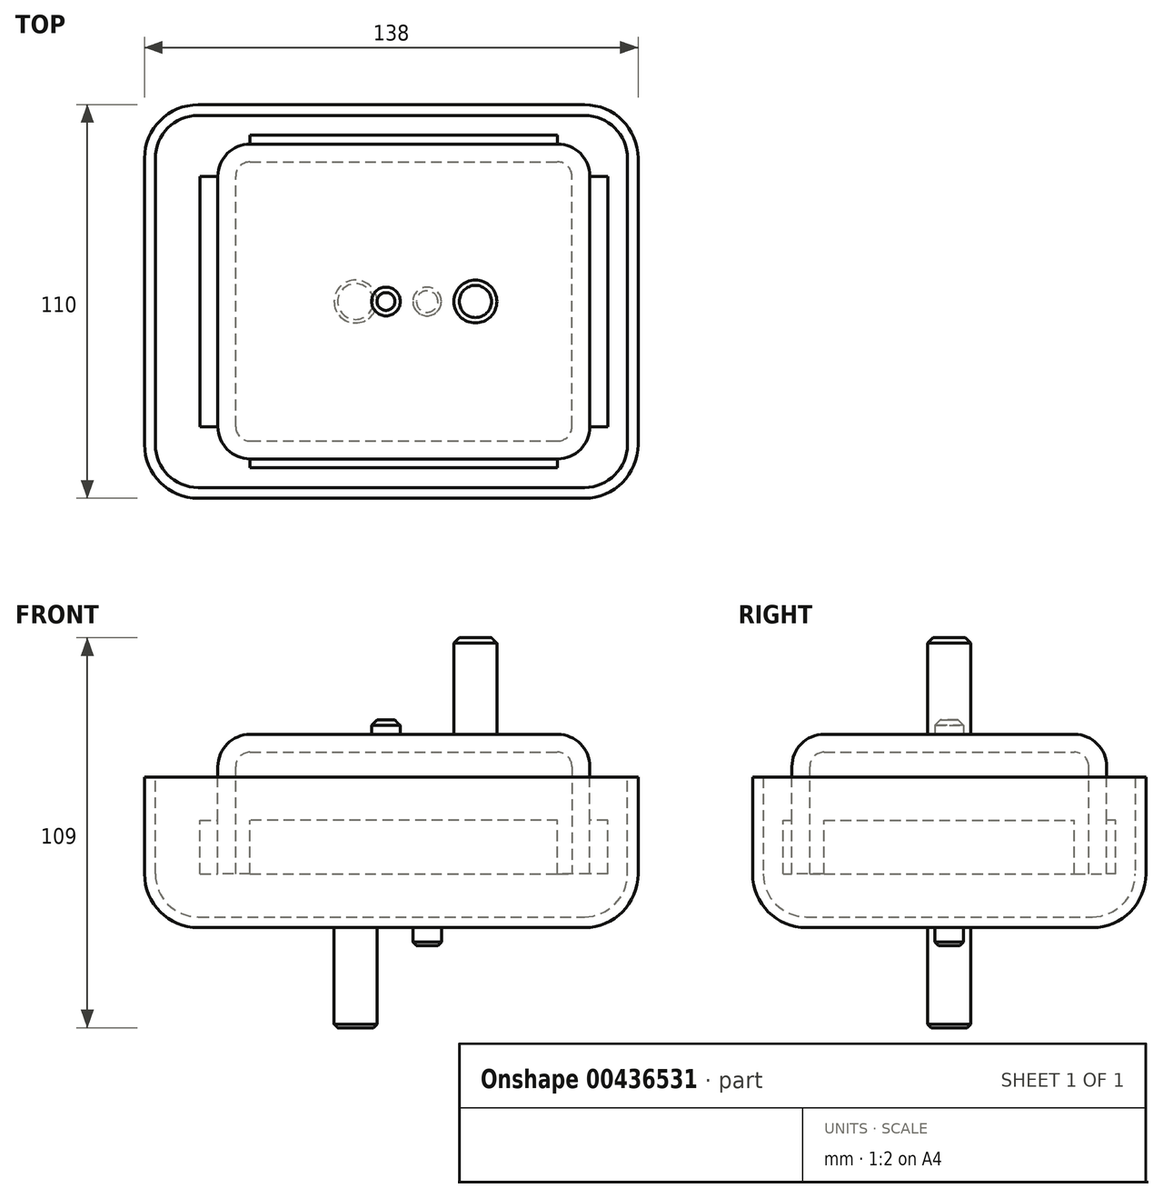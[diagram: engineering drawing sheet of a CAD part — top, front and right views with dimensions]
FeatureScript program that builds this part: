
annotation { "Feature Type Name" : "Feature", "Feature Type Description" : "" }
export const myFeature = defineFeature(function(context is Context, id is Id, definition is map)
    precondition{}
    {
        {
            var Q0;
            Q0=qCreatedBy(makeId("Top.planeOp"),FACE);
            var sketch = newSketch(context, id + "F0", { "sketchPlane" : qUnion([Q0])});
            skLineSegment(sketch, "E0.bottom", {"start": v(54, -55) * mm, "end": v(-54, -55) * mm});
            skLineSegment(sketch, "E0.top", {"start": v(54, 55) * mm, "end": v(-54, 55) * mm});
            skLineSegment(sketch, "E0.left", {"start": v(69, -40) * mm, "end": v(69, 40) * mm});
            skLineSegment(sketch, "E0.right", {"start": v(-69, -40) * mm, "end": v(-69, 40) * mm});
            skPoint(sketch, "E0.middle", {"position": v(0, 0) * mm});
            skPoint(sketch, "E1.visualSharp", {"position": v(-69, 55) * mm});
            skArc(sketch, "E1.filletArc", {"start": v(-54, 55) * mm, "mid": v(-64.6, 50.6) * mm, "end": v(-69, 40) * mm});
            skPoint(sketch, "E2.visualSharp", {"position": v(69, 55) * mm});
            skArc(sketch, "E2.filletArc", {"start": v(69, 40) * mm, "mid": v(64.6, 50.6) * mm, "end": v(54, 55) * mm});
            skPoint(sketch, "E3.visualSharp", {"position": v(69, -55) * mm});
            skArc(sketch, "E3.filletArc", {"start": v(54, -55) * mm, "mid": v(64.6, -50.6) * mm, "end": v(69, -40) * mm});
            skPoint(sketch, "E4.visualSharp", {"position": v(-69, -55) * mm});
            skArc(sketch, "E4.filletArc", {"start": v(-69, -40) * mm, "mid": v(-64.6, -50.6) * mm, "end": v(-54, -55) * mm});
            skSolve(sketch);
        }
        {
            var Q0;
            Q0 = qSketchRegion(id + "F0", true);
            extrude(context, id + "F1", {"entities" : qUnion([Q0]), "depth" : 42 * mm});
        }
        {
            var Q0;
            Q0=makeQuery(id+"F1.opExtrude","CAP_EDGE",EDGE,{"disambiguationData":[OSD([sQuery(id+"F0.wireOp",EDGE,"E0.bottom")])],"isStart":true});
            fillet(context, id + "F2", {"entities" : qUnion([Q0]), "radius" : 15 * mm, "tangentPropagation" : true, "allowEdgeOverflow" : false});
        }
        {
            var Q0;
            Q0=makeQuery(id+"F1.opExtrude","CAP_FACE",FACE,{"disambiguationData":[OSD([sQuery(id+"F0.wireOp",EDGE,"E0.bottom"),sQuery(id+"F0.wireOp",EDGE,"E0.top"),sQuery(id+"F0.wireOp",EDGE,"E0.left"),sQuery(id+"F0.wireOp",EDGE,"E0.right"),sQuery(id+"F0.wireOp",EDGE,"E1.filletArc"),sQuery(id+"F0.wireOp",EDGE,"E2.filletArc"),sQuery(id+"F0.wireOp",EDGE,"E3.filletArc"),sQuery(id+"F0.wireOp",EDGE,"E4.filletArc")])],"isStart":false});
            shell(context, id + "F3", {"entities" : qUnion([Q0]), "thickness" : 3 * mm});
        }
        {
            var Q0;
            Q0=makeQuery(id+"F1.opExtrude","CAP_FACE",FACE,{"disambiguationData":[OSD([sQuery(id+"F0.wireOp",EDGE,"E0.bottom"),sQuery(id+"F0.wireOp",EDGE,"E0.top"),sQuery(id+"F0.wireOp",EDGE,"E0.left"),sQuery(id+"F0.wireOp",EDGE,"E0.right"),sQuery(id+"F0.wireOp",EDGE,"E1.filletArc"),sQuery(id+"F0.wireOp",EDGE,"E2.filletArc"),sQuery(id+"F0.wireOp",EDGE,"E3.filletArc"),sQuery(id+"F0.wireOp",EDGE,"E4.filletArc")])],"isStart":true});
            var sketch = newSketch(context, id + "F4", { "sketchPlane" : qUnion([Q0])});
            skCircle(sketch, "E5", {"center": v(-10, 0) * mm, "radius": 6 * mm});
            skCircle(sketch, "E6", {"center": v(10, 0) * mm, "radius": 4 * mm});
            skSolve(sketch);
        }
        {
            var Q0;
            Q0=makeQuery(id+"F4.imprint","IMPRINT",FACE,{"disambiguationData":[TD([[makeQuery(id+"F4.imprint","IMPRINT",EDGE,{"derivedFrom":sQuery(id+"F4.wireOp",EDGE,"E5")}),1.0]])]});
            extrude(context, id + "F5", {"entities" : qUnion([Q0]), "operationType" : NewBodyOperationType.ADD, "depth" : 28 * mm});
        }
        {
            var Q0;
            Q0=makeQuery(id+"F4.imprint","IMPRINT",FACE,{"disambiguationData":[TD([[makeQuery(id+"F4.imprint","IMPRINT",EDGE,{"derivedFrom":sQuery(id+"F4.wireOp",EDGE,"E6")}),1.0]])]});
            extrude(context, id + "F6", {"entities" : qUnion([Q0]), "operationType" : NewBodyOperationType.ADD, "depth" : 5 * mm});
        }
        {
            var Q0;
            Q0=makeQuery(id+"F6.opExtrude","CAP_EDGE",EDGE,{"disambiguationData":[OSD([sQuery(id+"F4.wireOp",EDGE,"E6")])],"isStart":false});
            var Q1;
            Q1=makeQuery(id+"F5.opExtrude","CAP_EDGE",EDGE,{"disambiguationData":[OSD([sQuery(id+"F4.wireOp",EDGE,"E5")])],"isStart":false});
            chamfer(context, id + "F7", {"entities" : qUnion([Q0, Q1]), "width" : 1 * mm, "tangentPropagation" : true});
        }
        {
            var Q0;
            Q0=qCreatedBy(makeId("Top.planeOp"),FACE);
            cPlane(context, id + "F8", {"entities" : qUnion([Q0]), "cplaneType" : CPlaneType.OFFSET, "offset" : 54 * mm, "width" : 150 * mm, "height" : 150 * mm});
        }
        {
            var Q0;
            Q0=qCreatedBy(id+"F8.planeOp",FACE);
            var sketch = newSketch(context, id + "F9", { "sketchPlane" : qUnion([Q0])});
            skLineSegment(sketch, "E7.bottom", {"start": v(-39.5, -44) * mm, "end": v(46.5, -44) * mm});
            skLineSegment(sketch, "E7.top", {"start": v(-39.5, 44) * mm, "end": v(46.5, 44) * mm});
            skLineSegment(sketch, "E7.left", {"start": v(-48.5, -35) * mm, "end": v(-48.5, 35) * mm});
            skLineSegment(sketch, "E7.right", {"start": v(55.5, -35) * mm, "end": v(55.5, 35) * mm});
            skPoint(sketch, "E8.visualSharp", {"position": v(-48.5, 44) * mm});
            skArc(sketch, "E8.filletArc", {"start": v(-39.5, 44) * mm, "mid": v(-45.86, 41.36) * mm, "end": v(-48.5, 35) * mm});
            skPoint(sketch, "E9.visualSharp", {"position": v(55.5, 44) * mm});
            skArc(sketch, "E9.filletArc", {"start": v(55.5, 35) * mm, "mid": v(52.86, 41.36) * mm, "end": v(46.5, 44) * mm});
            skPoint(sketch, "E10.visualSharp", {"position": v(55.5, -44) * mm});
            skArc(sketch, "E10.filletArc", {"start": v(46.5, -44) * mm, "mid": v(52.86, -41.36) * mm, "end": v(55.5, -35) * mm});
            skPoint(sketch, "E11.visualSharp", {"position": v(-48.5, -44) * mm});
            skArc(sketch, "E11.filletArc", {"start": v(-48.5, -35) * mm, "mid": v(-45.86, -41.36) * mm, "end": v(-39.5, -44) * mm});
            skSolve(sketch);
        }
        {
            var Q0;
            Q0 = qSketchRegion(id + "F9", true);
            extrude(context, id + "F10", {"entities" : qUnion([Q0]), "oppositeDirection" : true, "depth" : 39 * mm});
        }
        {
            var Q0;
            Q0=makeQuery(id+"F10.opExtrude","CAP_EDGE",EDGE,{"disambiguationData":[OSD([sQuery(id+"F9.wireOp",EDGE,"E7.left")])],"isStart":true});
            fillet(context, id + "F11", {"entities" : qUnion([Q0]), "radius" : 9 * mm, "tangentPropagation" : true, "allowEdgeOverflow" : false});
        }
        {
            var Q0;
            Q0=makeQuery(id+"F10.opExtrude","CAP_FACE",FACE,{"disambiguationData":[OSD([sQuery(id+"F9.wireOp",EDGE,"E7.bottom"),sQuery(id+"F9.wireOp",EDGE,"E7.top"),sQuery(id+"F9.wireOp",EDGE,"E7.left"),sQuery(id+"F9.wireOp",EDGE,"E7.right"),sQuery(id+"F9.wireOp",EDGE,"E8.filletArc"),sQuery(id+"F9.wireOp",EDGE,"E9.filletArc"),sQuery(id+"F9.wireOp",EDGE,"E10.filletArc"),sQuery(id+"F9.wireOp",EDGE,"E11.filletArc")])],"isStart":false});
            shell(context, id + "F12", {"entities" : qUnion([Q0]), "thickness" : 5 * mm});
        }
        {
            var Q0;
            Q0=makeQuery(id+"F10.opExtrude","SWEPT_FACE",FACE,{"disambiguationData":[OSD([sQuery(id+"F9.wireOp",EDGE,"E7.bottom")])]});
            var sketch = newSketch(context, id + "F13", { "sketchPlane" : qUnion([Q0])});
            skLineSegment(sketch, "E12.bottom", {"start": v(-39.5, 15) * mm, "end": v(46.5, 15) * mm});
            skLineSegment(sketch, "E12.top", {"start": v(-39.5, 30) * mm, "end": v(46.5, 30) * mm});
            skLineSegment(sketch, "E12.left", {"start": v(-39.5, 15) * mm, "end": v(-39.5, 30) * mm});
            skLineSegment(sketch, "E12.right", {"start": v(46.5, 15) * mm, "end": v(46.5, 30) * mm});
            skSolve(sketch);
        }
        {
            var Q0;
            Q0 = qSketchRegion(id + "F13", true);
            extrude(context, id + "F14", {"entities" : qUnion([Q0]), "operationType" : NewBodyOperationType.ADD, "depth" : 2.5 * mm});
        }
        {
            var Q0;
            Q0=makeQuery(id+"F10.opExtrude","SWEPT_FACE",FACE,{"disambiguationData":[OSD([sQuery(id+"F9.wireOp",EDGE,"E7.top")])]});
            var sketch = newSketch(context, id + "F15", { "sketchPlane" : qUnion([Q0])});
            skLineSegment(sketch, "E13.bottom", {"start": v(-46.5, 15) * mm, "end": v(39.5, 15) * mm});
            skLineSegment(sketch, "E13.top", {"start": v(-46.5, 30) * mm, "end": v(39.5, 30) * mm});
            skLineSegment(sketch, "E13.left", {"start": v(-46.5, 15) * mm, "end": v(-46.5, 30) * mm});
            skLineSegment(sketch, "E13.right", {"start": v(39.5, 15) * mm, "end": v(39.5, 30) * mm});
            skSolve(sketch);
        }
        {
            var Q0;
            Q0 = qSketchRegion(id + "F15", true);
            extrude(context, id + "F16", {"entities" : qUnion([Q0]), "operationType" : NewBodyOperationType.ADD, "depth" : 2.5 * mm});
        }
        {
            var Q0;
            Q0=makeQuery(id+"F10.opExtrude","SWEPT_FACE",FACE,{"disambiguationData":[OSD([sQuery(id+"F9.wireOp",EDGE,"E7.left")])]});
            var sketch = newSketch(context, id + "F17", { "sketchPlane" : qUnion([Q0])});
            skLineSegment(sketch, "E14.bottom", {"start": v(35, 15) * mm, "end": v(-35, 15) * mm});
            skLineSegment(sketch, "E14.top", {"start": v(35, 30) * mm, "end": v(-35, 30) * mm});
            skLineSegment(sketch, "E14.left", {"start": v(35, 15) * mm, "end": v(35, 30) * mm});
            skLineSegment(sketch, "E14.right", {"start": v(-35, 15) * mm, "end": v(-35, 30) * mm});
            skSolve(sketch);
        }
        {
            var Q0;
            Q0 = qSketchRegion(id + "F17", true);
            extrude(context, id + "F18", {"entities" : qUnion([Q0]), "operationType" : NewBodyOperationType.ADD, "depth" : 5 * mm});
        }
        {
            var Q0;
            Q0=makeQuery(id+"F10.opExtrude","SWEPT_FACE",FACE,{"disambiguationData":[OSD([sQuery(id+"F9.wireOp",EDGE,"E7.right")])]});
            var sketch = newSketch(context, id + "F19", { "sketchPlane" : qUnion([Q0])});
            skLineSegment(sketch, "E15.bottom", {"start": v(-35, 15) * mm, "end": v(35, 15) * mm});
            skLineSegment(sketch, "E15.top", {"start": v(-35, 30) * mm, "end": v(35, 30) * mm});
            skLineSegment(sketch, "E15.left", {"start": v(-35, 15) * mm, "end": v(-35, 30) * mm});
            skLineSegment(sketch, "E15.right", {"start": v(35, 15) * mm, "end": v(35, 30) * mm});
            skSolve(sketch);
        }
        {
            var Q0;
            Q0 = qSketchRegion(id + "F19", true);
            extrude(context, id + "F20", {"entities" : qUnion([Q0]), "operationType" : NewBodyOperationType.ADD, "depth" : 5 * mm});
        }
        {
            var Q0;
            Q0=makeQuery(id+"F10.opExtrude","CAP_FACE",FACE,{"disambiguationData":[OSD([sQuery(id+"F9.wireOp",EDGE,"E7.bottom"),sQuery(id+"F9.wireOp",EDGE,"E7.top"),sQuery(id+"F9.wireOp",EDGE,"E7.left"),sQuery(id+"F9.wireOp",EDGE,"E7.right"),sQuery(id+"F9.wireOp",EDGE,"E8.filletArc"),sQuery(id+"F9.wireOp",EDGE,"E9.filletArc"),sQuery(id+"F9.wireOp",EDGE,"E10.filletArc"),sQuery(id+"F9.wireOp",EDGE,"E11.filletArc")])],"isStart":true});
            var sketch = newSketch(context, id + "F21", { "sketchPlane" : qUnion([Q0])});
            skCircle(sketch, "E16", {"center": v(23.5, 0) * mm, "radius": 6 * mm});
            skCircle(sketch, "E17", {"center": v(-1.5, 0) * mm, "radius": 4 * mm});
            skSolve(sketch);
        }
        {
            var Q0;
            Q0=makeQuery(id+"F21.imprint","IMPRINT",FACE,{"disambiguationData":[TD([[makeQuery(id+"F21.imprint","IMPRINT",EDGE,{"derivedFrom":sQuery(id+"F21.wireOp",EDGE,"E16")}),1.0]])]});
            extrude(context, id + "F22", {"entities" : qUnion([Q0]), "operationType" : NewBodyOperationType.ADD, "depth" : 27 * mm});
        }
        {
            var Q0;
            Q0=makeQuery(id+"F21.imprint","IMPRINT",FACE,{"disambiguationData":[TD([[makeQuery(id+"F21.imprint","IMPRINT",EDGE,{"derivedFrom":sQuery(id+"F21.wireOp",EDGE,"E17")}),1.0]])]});
            extrude(context, id + "F23", {"entities" : qUnion([Q0]), "operationType" : NewBodyOperationType.ADD, "depth" : 4 * mm});
        }
        {
            var Q0;
            Q0=makeQuery(id+"F22.opExtrude","CAP_EDGE",EDGE,{"disambiguationData":[OSD([sQuery(id+"F21.wireOp",EDGE,"E16")])],"isStart":false});
            var Q1;
            Q1=makeQuery(id+"F23.opExtrude","CAP_EDGE",EDGE,{"disambiguationData":[OSD([sQuery(id+"F21.wireOp",EDGE,"E17")])],"isStart":false});
            chamfer(context, id + "F24", {"entities" : qUnion([Q0, Q1]), "width" : 1.5 * mm, "tangentPropagation" : true});
        }
    });
